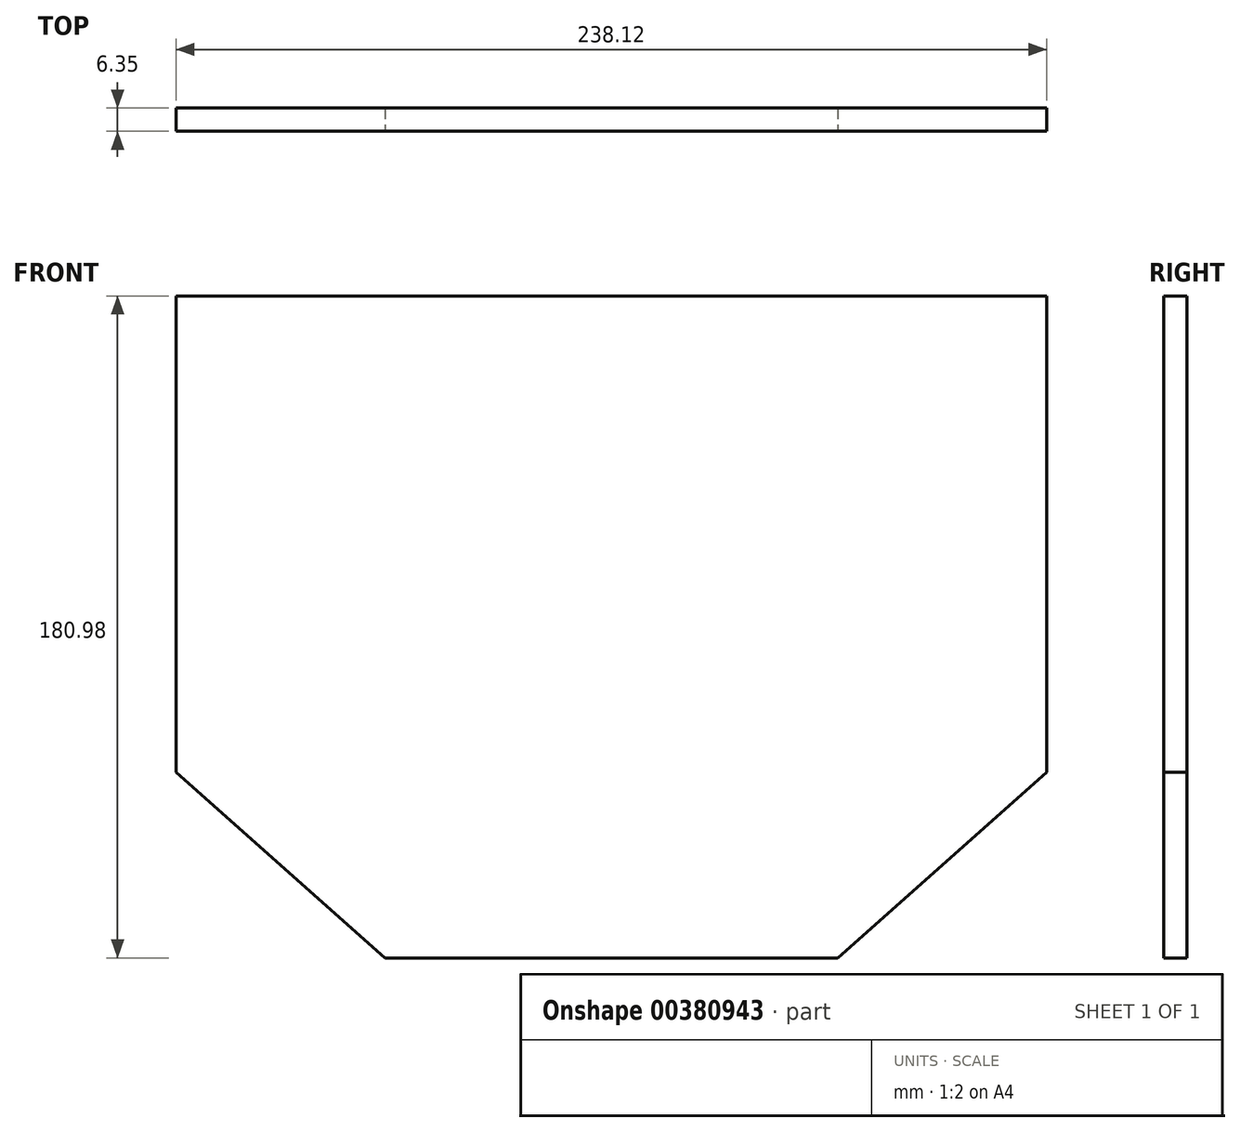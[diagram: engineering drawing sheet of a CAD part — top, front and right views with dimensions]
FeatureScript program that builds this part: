
annotation { "Feature Type Name" : "Feature", "Feature Type Description" : "" }
export const myFeature = defineFeature(function(context is Context, id is Id, definition is map)
    precondition{}
    {
        {
            var Q0;
            Q0=qCreatedBy(makeId("Front.planeOp"),FACE);
            var sketch = newSketch(context, id + "F0", { "sketchPlane" : qUnion([Q0])});
            skLineSegment(sketch, "E0.bottom", {"start": v(119.06, 90.49) * mm, "end": v(-119.06, 90.49) * mm});
            skLineSegment(sketch, "E0.top", {"start": v(96.01, -90.49) * mm, "end": v(-88.14, -90.49) * mm});
            skLineSegment(sketch, "E0.left", {"start": v(119.06, 90.49) * mm, "end": v(119.06, -65) * mm});
            skLineSegment(sketch, "E0.right", {"start": v(-119.06, 90.49) * mm, "end": v(-119.06, -59.1) * mm});
            skPoint(sketch, "E0.middle", {"position": v(0, 0) * mm});
            skPoint(sketch, "E1.orphan", {"position": v(-119.06, -90.49) * mm});
            skPoint(sketch, "E2.orphan", {"position": v(119.06, -90.49) * mm});
            skLineSegment(sketch, "E3", {"start": v(-119.06, -59.1) * mm, "end": v(-119.06, -90.49) * mm});
            skLineSegment(sketch, "E4", {"start": v(-88.14, -90.49) * mm, "end": v(-119.06, -90.49) * mm});
            skLineSegment(sketch, "E5", {"start": v(96.01, -90.49) * mm, "end": v(119.06, -90.49) * mm});
            skLineSegment(sketch, "E6", {"start": v(119.06, -65) * mm, "end": v(119.06, -90.49) * mm});
            skSolve(sketch);
        }
        {
            var Q0;
            Q0=qSketchRegion(id+"F0",true);
            extrude(context, id + "F1", {"entities" : qUnion([Q0]), "depth" : 6.35 * mm});
        }
        {
            var Q0;
            Q0=makeQuery(id+"F1.opExtrude","CAP_FACE",FACE,{"disambiguationData":[OSD([sQuery(id+"F0.wireOp",EDGE,"E0.bottom"),sQuery(id+"F0.wireOp",EDGE,"E0.top"),sQuery(id+"F0.wireOp",EDGE,"E0.left"),sQuery(id+"F0.wireOp",EDGE,"E0.right"),sQuery(id+"F0.wireOp",EDGE,"E3"),sQuery(id+"F0.wireOp",EDGE,"E4"),sQuery(id+"F0.wireOp",EDGE,"E5"),sQuery(id+"F0.wireOp",EDGE,"E6")])],"isStart":false});
            var sketch = newSketch(context, id + "F2", { "sketchPlane" : qUnion([Q0])});
            skLineSegment(sketch, "E7", {"start": v(-119.06, -39.69) * mm, "end": v(-61.91, -90.49) * mm});
            skLineSegment(sketch, "E8", {"start": v(61.91, -90.49) * mm, "end": v(119.06, -39.69) * mm});
            skLineSegment(sketch, "E9", {"start": v(-119.06, -39.69) * mm, "end": v(-119.06, -90.49) * mm});
            skLineSegment(sketch, "E10", {"start": v(-119.06, -90.49) * mm, "end": v(-61.91, -90.49) * mm});
            skLineSegment(sketch, "E11", {"start": v(61.91, -90.49) * mm, "end": v(119.06, -90.49) * mm});
            skLineSegment(sketch, "E12", {"start": v(119.06, -90.49) * mm, "end": v(119.06, -39.69) * mm});
            skSolve(sketch);
        }
        {
            var Q0;
            Q0=qSketchRegion(id+"F2",true);
            extrude(context, id + "F3", {"entities" : qUnion([Q0]), "operationType" : NewBodyOperationType.REMOVE, "oppositeDirection" : true, "depth" : 25.4 * mm});
        }
    });
